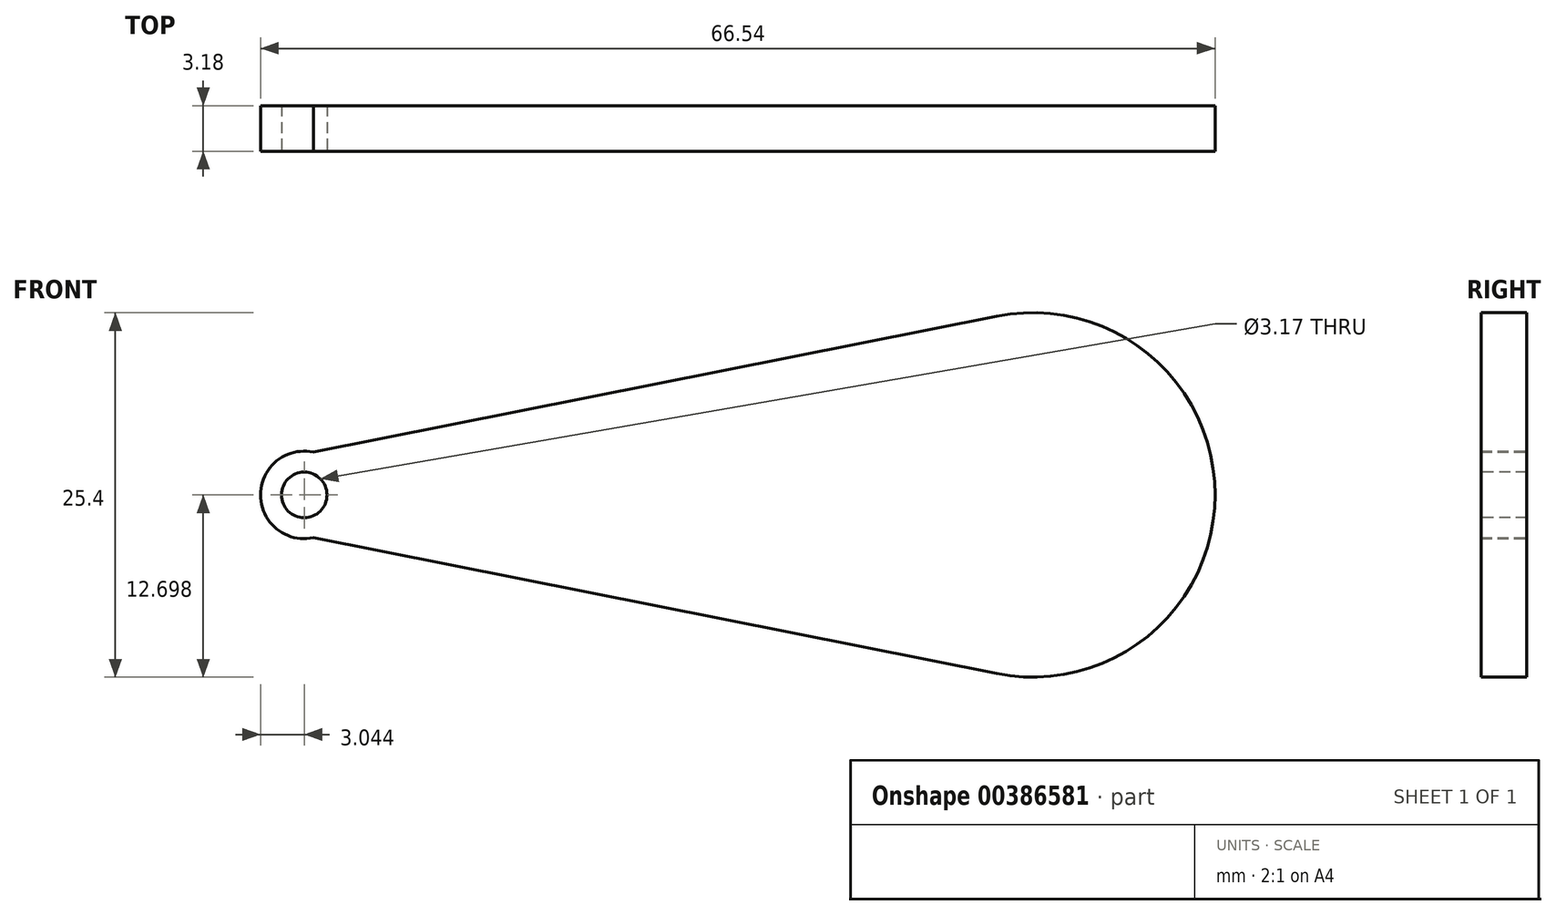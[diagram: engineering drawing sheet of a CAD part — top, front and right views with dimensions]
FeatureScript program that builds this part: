
annotation { "Feature Type Name" : "Feature", "Feature Type Description" : "" }
export const myFeature = defineFeature(function(context is Context, id is Id, definition is map)
    precondition{}
    {
        {
            var Q0;
            Q0=qCreatedBy(makeId("Front.planeOp"),FACE);
            var sketch = newSketch(context, id + "F0", { "sketchPlane" : qUnion([Q0])});
            skArc(sketch, "E0", {"start": v(23.12, -5.78) * mm, "mid": v(38.35, 6.67) * mm, "end": v(23.12, 19.11) * mm});
            skArc(sketch, "E1", {"start": v(-24.51, 9.65) * mm, "mid": v(-28.2, 6.67) * mm, "end": v(-24.51, 3.69) * mm});
            skLineSegment(sketch, "E2", {"start": v(23.24, -5.8) * mm, "end": v(-24.51, 3.69) * mm});
            skLineSegment(sketch, "E3", {"start": v(-25.15, 6.67) * mm, "end": v(25.65, 6.67) * mm});
            skLineSegment(sketch, "E4.MirrorCS", {"start": v(23.24, 19.14) * mm, "end": v(-24.51, 9.65) * mm});
            skSolve(sketch);
        }
        {
            var Q0;
            Q0 = qSketchRegion(id + "F0", true);
            extrude(context, id + "F1", {"entities" : qUnion([Q0]), "depth" : 3.17 * mm});
        }
        {
            var Q0;
            Q0=makeQuery(id+"F1.opExtrude","CAP_FACE",FACE,{"disambiguationData":[OSD([sQuery(id+"F0.wireOp",EDGE,"E0"),sQuery(id+"F0.wireOp",EDGE,"E1"),sQuery(id+"F0.wireOp",EDGE,"E2"),sQuery(id+"F0.wireOp",EDGE,"E4.MirrorCS")])],"isStart":false});
            var sketch = newSketch(context, id + "F2", { "sketchPlane" : qUnion([Q0])});
            skPoint(sketch, "E5", {"position": v(-25.15, 6.67) * mm});
            skSolve(sketch);
        }
        {
            var Q0;
            Q0=sQuery(id+"F2.wireOp",VERTEX,"E5");
            var Q1;
            Q1=makeQuery(id+"F1.opExtrude","SWEPT_BODY",BODY,{"disambiguationData":[OSD([sQuery(id+"F0.wireOp",EDGE,"E0"),sQuery(id+"F0.wireOp",EDGE,"E1"),sQuery(id+"F0.wireOp",EDGE,"E2"),sQuery(id+"F0.wireOp",EDGE,"E4.MirrorCS")])]});
            hole(context, id + "F3", {"style" : HoleStyle.SIMPLE, "endStyle" : HoleEndStyle.THROUGH, "holeDiameter" : 3.17 * mm, "isTappedThrough" : true, "tappedDepth" : 12.7 * mm, "tapClearance" : 3, "locations" : qUnion([Q0]), "scope" : qUnion([Q1])});
        }
    });
